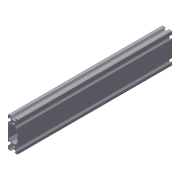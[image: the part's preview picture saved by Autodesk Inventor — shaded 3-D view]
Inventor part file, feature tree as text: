
AUTODESK INVENTOR PART (.ipt)
format: ipt  version: 2013 (Build 170138000, 138)  size: 452,096 bytes
history: native  units: in
note: dims shown in document units (in); Inventor stores cm internally (conversion verified against a paired STEP export)
features: other x1, extrude x1, sketch x1
ambient origin geometry x8: Origin, YZ Plane, XZ Plane, XY Plane, X Axis, Y Axis, Z Axis, Center Point
bodies: Solid1 (feature_tree)
feature tree (3):
  other  "Blocks"
  extrude  "Extrusion1"  [1 undecoded]
  sketch  "Sketch1"  dims[d1=0.0in]
note: 1 required parameter value undecoded (feature->parameter linkage not recoverable at this tier; creation-order binding heuristic only, values carry confidence <= 0.55)
